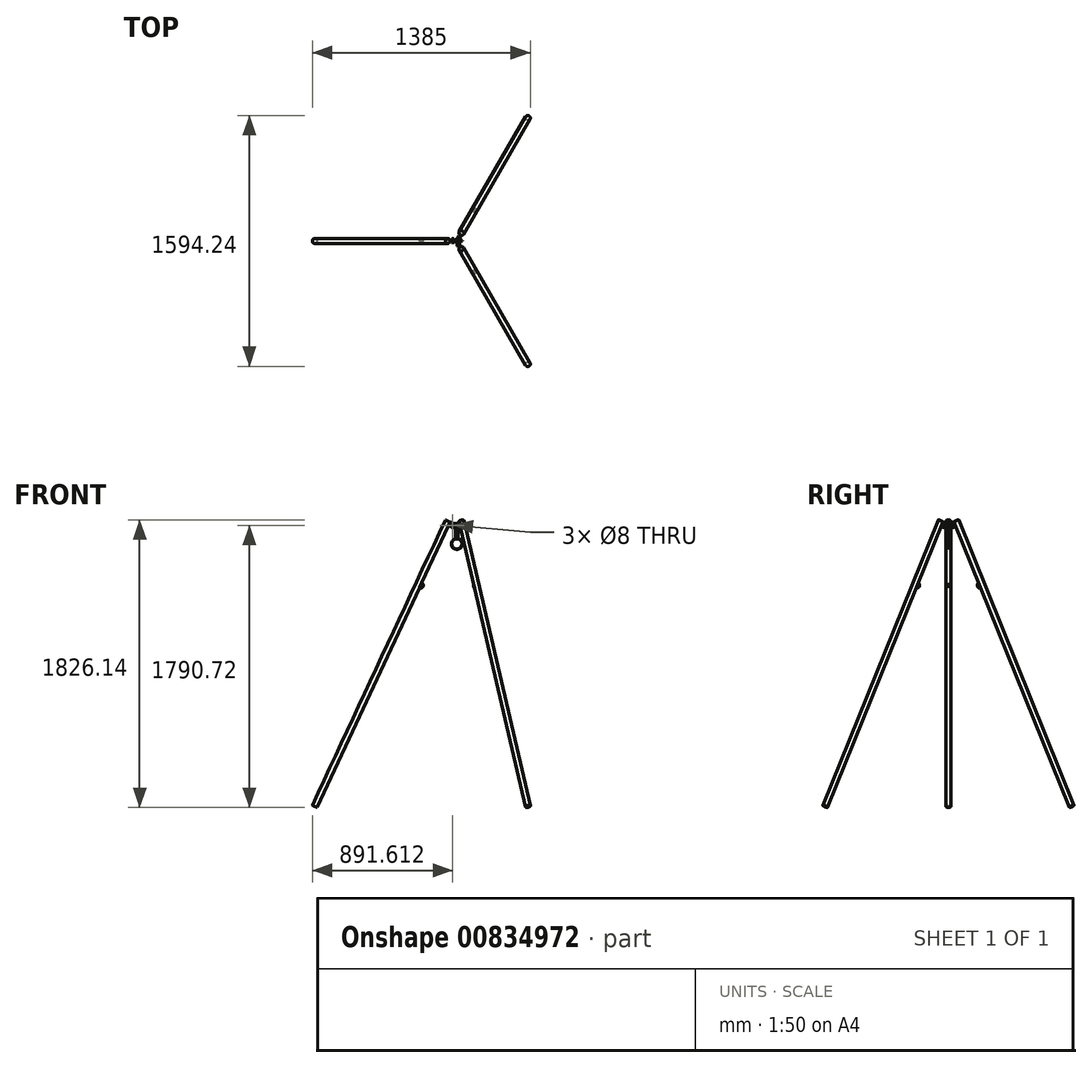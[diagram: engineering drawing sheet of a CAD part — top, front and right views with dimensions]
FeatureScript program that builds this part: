
annotation { "Feature Type Name" : "Feature", "Feature Type Description" : "" }
export const myFeature = defineFeature(function(context is Context, id is Id, definition is map)
    precondition{}
    {
        {
            assignVariable(context, id + "F0", {"variableType" : VariableType.LENGTH, "name" : "PipeLength", "lengthValue" : 2000 * mm});
        }
        {
            assignVariable(context, id + "F1", {"variableType" : VariableType.ANGLE, "name" : "LegAngle", "angleValue" : 25 * degree});
        }
        {
            var Q0;
            Q0=qCreatedBy(makeId("Right.planeOp"),FACE);
            var sketch = newSketch(context, id + "F2", { "sketchPlane" : qUnion([Q0])});
            skLineSegment(sketch, "E0", {"start": v(0, 0) * mm, "end": v(-174.54, 0) * mm, "construction": true});
            skLineSegment(sketch, "E1", {"start": v(0, 0) * mm, "end": v(0, 119.44) * mm, "construction": true});
            skSolve(sketch);
        }
        {
            var Q0;
            Q0=sQuery(id+"F2.wireOp",EDGE,"E0");
            var Q1;
            Q1=sQuery(id+"F2.wireOp",VERTEX,"E1.end");
            cPlane(context, id + "F3", {"entities" : qUnion([Q0, Q1]), "cplaneType" : CPlaneType.LINE_ANGLE, "offset" : 25 * mm, "angle" : 90 * degree - getVariable(context, 'LegAngle'), "width" : 150 * mm, "height" : 150 * mm});
        }
        {
            var Q0;
            Q0=qCreatedBy(id+"F3.planeOp",FACE);
            var sketch = newSketch(context, id + "F4", { "sketchPlane" : qUnion([Q0])});
            skCircle(sketch, "E2", {"center": v(-64, 0) * mm, "radius": 16 * mm});
            skSolve(sketch);
        }
        {
            var Q0;
            Q0=qSketchRegion(id+"F4",true);
            extrude(context, id + "F5", {"entities" : qUnion([Q0]), "depth" : getVariable(context, 'PipeLength'), "offsetDistance" : 25 * mm});
        }
        {
            var Q0;
            Q0=qCreatedBy(makeId("Front.planeOp"),FACE);
            var sketch = newSketch(context, id + "F6", { "sketchPlane" : qUnion([Q0])});
            skCircle(sketch, "E3", {"center": v(-26.13, -1.6) * mm, "radius": 4 * mm});
            skArc(sketch, "E4", {"start": v(-31.41, -12.94) * mm, "mid": v(-14.8, -6.9) * mm, "end": v(-20.85, 9.72) * mm});
            skLineSegment(sketch, "E5", {"start": v(-43.5, 20.29) * mm, "end": v(-888.74, -1792.33) * mm, "construction": true});
            skLineSegment(sketch, "E6.0", {"start": v(-43.5, 20.29) * mm, "end": v(-72.5, 33.8) * mm, "construction": true});
            skLineSegment(sketch, "E7", {"start": v(-20.85, 9.72) * mm, "end": v(-43.5, 20.29) * mm});
            skLineSegment(sketch, "E8", {"start": v(-31.41, -12.94) * mm, "end": v(-54.07, -2.37) * mm});
            skLineSegment(sketch, "E9", {"start": v(-54.07, -2.37) * mm, "end": v(-43.5, 20.29) * mm});
            skSolve(sketch);
        }
        {
            var Q0;
            Q0 = qSketchRegion(id + "F6", true);
            extrude(context, id + "F7", {"entities" : qUnion([Q0]), "operationType" : NewBodyOperationType.ADD, "endBound" : BoundingType.SYMMETRIC, "depth" : 3 * mm, "offsetDistance" : 25 * mm});
        }
        {
            var Q0;
            Q0=qCreatedBy(makeId("Front.planeOp"),FACE);
            var sketch = newSketch(context, id + "F8", { "sketchPlane" : qUnion([Q0])});
            skLineSegment(sketch, "E10", {"start": v(-43.5, 20.29) * mm, "end": v(-888.74, -1792.33) * mm, "construction": true});
            skArc(sketch, "E11", {"start": v(-224.38, -367.61) * mm, "mid": v(-217.13, -387.55) * mm, "end": v(-237.06, -394.8) * mm});
            skArc(sketch, "E12", {"start": v(-223.12, -364.9) * mm, "mid": v(-214.4, -388.82) * mm, "end": v(-238.33, -397.52) * mm});
            skLineSegment(sketch, "E13", {"start": v(-223.12, -364.9) * mm, "end": v(-224.38, -367.61) * mm});
            skLineSegment(sketch, "E14", {"start": v(-237.06, -394.8) * mm, "end": v(-238.33, -397.52) * mm});
            skSolve(sketch);
        }
        {
            var Q0;
            Q0 = qSketchRegion(id + "F8", true);
            extrude(context, id + "F9", {"entities" : qUnion([Q0]), "endBound" : BoundingType.SYMMETRIC, "depth" : 3 * mm, "offsetDistance" : 25 * mm});
        }
        {
            var Q0;
            Q0=makeQuery(id+"F5.opExtrude","SWEPT_BODY",BODY,{"disambiguationData":[OSD([sQuery(id+"F4.wireOp",EDGE,"E2")])]});
            var Q1;
            Q1=makeQuery(id+"F7.opExtrude","SWEPT_BODY",BODY,{"disambiguationData":[OSD([sQuery(id+"F6.wireOp",EDGE,"E3"),sQuery(id+"F6.wireOp",EDGE,"E4"),sQuery(id+"F6.wireOp",EDGE,"E7"),sQuery(id+"F6.wireOp",EDGE,"E8"),sQuery(id+"F6.wireOp",EDGE,"E9")])]});
            var Q2;
            Q2=makeQuery(id+"F9.opExtrude","SWEPT_BODY",BODY,{"disambiguationData":[OSD([sQuery(id+"F8.wireOp",EDGE,"E11"),sQuery(id+"F8.wireOp",EDGE,"E12"),sQuery(id+"F8.wireOp",EDGE,"E13"),sQuery(id+"F8.wireOp",EDGE,"E14")])]});
            var Q3;
            Q3=sQuery(id+"F2.wireOp",EDGE,"E1");
            circularPattern(context, id + "F10", {"entities" : qUnion([Q0, Q1, Q2]), "axis" : qUnion([Q3]), "angle" : 360 * degree, "instanceCount" : 3, "equalSpace" : true});
        }
        {
            var Q0;
            Q0=qCreatedBy(makeId("Top.planeOp"),FACE);
            var sketch = newSketch(context, id + "F11", { "sketchPlane" : qUnion([Q0])});
            skLineSegment(sketch, "E15", {"start": v(-33.63, 1.5) * mm, "end": v(-13.63, 1.5) * mm});
            skLineSegment(sketch, "E16", {"start": v(-13.63, 1.5) * mm, "end": v(5.51, 12.55) * mm});
            skLineSegment(sketch, "E17", {"start": v(5.51, 12.55) * mm, "end": v(15.51, 29.87) * mm});
            skLineSegment(sketch, "E18", {"start": v(15.51, 29.87) * mm, "end": v(12.92, 31.37) * mm});
            skLineSegment(sketch, "E19", {"start": v(12.92, 31.37) * mm, "end": v(3.32, 14.75) * mm});
            skLineSegment(sketch, "E20", {"start": v(3.32, 14.75) * mm, "end": v(-14.43, 4.5) * mm});
            skLineSegment(sketch, "E21", {"start": v(-14.43, 4.5) * mm, "end": v(-33.63, 4.5) * mm});
            skLineSegment(sketch, "E22", {"start": v(-33.63, 4.5) * mm, "end": v(-33.63, 1.5) * mm});
            skLineSegment(sketch, "E23", {"start": v(-13.63, 1.5) * mm, "end": v(-13.63, -1.5) * mm, "construction": true});
            skLineSegment(sketch, "E24", {"start": v(8.11, 11.05) * mm, "end": v(5.51, 12.55) * mm, "construction": true});
            skSolve(sketch);
        }
        {
            var Q0;
            Q0 = qSketchRegion(id + "F11", true);
            extrude(context, id + "F12", {"entities" : qUnion([Q0]), "endBound" : BoundingType.SYMMETRIC, "depth" : 25 * mm, "offsetDistance" : 25 * mm});
        }
        {
            var Q0;
            Q0=makeQuery(id+"F12.opExtrude","SWEPT_FACE",FACE,{"disambiguationData":[OSD([sQuery(id+"F11.wireOp",EDGE,"E15")])]});
            var sketch = newSketch(context, id + "F13", { "sketchPlane" : qUnion([Q0])});
            skCircle(sketch, "E25.0", {"center": v(-26.13, -1.6) * mm, "radius": 4 * mm});
            skSolve(sketch);
        }
        {
            var Q0;
            Q0 = qSketchRegion(id + "F13", true);
            extrude(context, id + "F14", {"entities" : qUnion([Q0]), "operationType" : NewBodyOperationType.REMOVE, "oppositeDirection" : true, "depth" : 25 * mm, "offsetDistance" : 25 * mm});
        }
        {
            var Q0;
            Q0=makeQuery(id+"F12.opExtrude","SWEPT_FACE",FACE,{"disambiguationData":[OSD([sQuery(id+"F11.wireOp",EDGE,"E17")])]});
            var sketch = newSketch(context, id + "F15", { "sketchPlane" : qUnion([Q0])});
            skCircle(sketch, "E26.0", {"center": v(26.13, -1.6) * mm, "radius": 4 * mm});
            skSolve(sketch);
        }
        {
            var Q0;
            Q0 = qSketchRegion(id + "F15", true);
            extrude(context, id + "F16", {"entities" : qUnion([Q0]), "operationType" : NewBodyOperationType.REMOVE, "oppositeDirection" : true, "depth" : 25 * mm, "offsetDistance" : 25 * mm});
        }
        {
            var Q0;
            Q0=makeQuery(id+"F12.opExtrude","SWEPT_BODY",BODY,{"disambiguationData":[OSD([sQuery(id+"F11.wireOp",EDGE,"E15"),sQuery(id+"F11.wireOp",EDGE,"E16"),sQuery(id+"F11.wireOp",EDGE,"E17"),sQuery(id+"F11.wireOp",EDGE,"E18"),sQuery(id+"F11.wireOp",EDGE,"E19"),sQuery(id+"F11.wireOp",EDGE,"E20"),sQuery(id+"F11.wireOp",EDGE,"E21"),sQuery(id+"F11.wireOp",EDGE,"E22")])]});
            var Q1;
            Q1=sQuery(id+"F2.wireOp",EDGE,"E1");
            circularPattern(context, id + "F17", {"entities" : qUnion([Q0]), "axis" : qUnion([Q1]), "angle" : 360 * degree, "instanceCount" : 3, "equalSpace" : true});
        }
        {
            var Q0;
            Q0=makeQuery(id+"F17.opPattern","COPY",FACE,{"derivedFrom":makeQuery(id+"F12.opExtrude","SWEPT_FACE",FACE,{"disambiguationData":[OSD([sQuery(id+"F11.wireOp",EDGE,"E19")])]}),"instanceName":"1"});
            var sketch = newSketch(context, id + "F18", { "sketchPlane" : qUnion([Q0])});
            skCircle(sketch, "E27.0", {"center": v(-26.13, -1.6) * mm, "radius": 4 * mm});
            skSolve(sketch);
        }
        {
            var Q0;
            Q0 = qSketchRegion(id + "F18", true);
            extrude(context, id + "F19", {"entities" : qUnion([Q0]), "oppositeDirection" : true, "depth" : (3 * 3 + 10) * mm, "offsetDistance" : 25 * mm});
        }
        {
            var Q0;
            Q0=makeQuery(id+"F19.opExtrude","CAP_FACE",FACE,{"disambiguationData":[OSD([sQuery(id+"F18.wireOp",EDGE,"E27.0")])],"isStart":true});
            var sketch = newSketch(context, id + "F20", { "sketchPlane" : qUnion([Q0])});
            skCircle(sketch, "E28.cCircle", {"center": v(-26.13, -1.6) * mm, "radius": 6.5 * mm, "construction": true});
            skLineSegment(sketch, "E28.0", {"start": v(-19.09, -4.2) * mm, "end": v(-24.86, -9) * mm});
            skLineSegment(sketch, "E28.1", {"start": v(-24.86, -9) * mm, "end": v(-31.9, -6.4) * mm});
            skLineSegment(sketch, "E28.2", {"start": v(-31.9, -6.4) * mm, "end": v(-33.17, 1) * mm});
            skLineSegment(sketch, "E28.3", {"start": v(-33.17, 1) * mm, "end": v(-27.4, 5.79) * mm});
            skLineSegment(sketch, "E28.4", {"start": v(-27.4, 5.79) * mm, "end": v(-20.36, 3.19) * mm});
            skLineSegment(sketch, "E28.5", {"start": v(-20.36, 3.19) * mm, "end": v(-19.09, -4.2) * mm});
            skPoint(sketch, "E28.0.midPoint", {"position": v(-21.97, -6.6) * mm});
            skSolve(sketch);
        }
        {
            var Q0;
            Q0 = qSketchRegion(id + "F20", true);
            extrude(context, id + "F21", {"entities" : qUnion([Q0]), "operationType" : NewBodyOperationType.ADD, "depth" : 6 * mm, "offsetDistance" : 25 * mm});
        }
        {
            var Q0;
            Q0=makeQuery(id+"F12.opExtrude","SWEPT_FACE",FACE,{"disambiguationData":[OSD([sQuery(id+"F11.wireOp",EDGE,"E21")])]});
            var sketch = newSketch(context, id + "F22", { "sketchPlane" : qUnion([Q0])});
            skCircle(sketch, "E29.0.0", {"center": v(26.13, -1.6) * mm, "radius": 4 * mm});
            skCircle(sketch, "E30.cCircle", {"center": v(26.13, -1.6) * mm, "radius": 6.5 * mm, "construction": true});
            skLineSegment(sketch, "E30.0", {"start": v(22.38, 4.9) * mm, "end": v(29.88, 4.9) * mm});
            skLineSegment(sketch, "E30.1", {"start": v(29.88, 4.9) * mm, "end": v(33.63, -1.6) * mm});
            skLineSegment(sketch, "E30.2", {"start": v(33.63, -1.6) * mm, "end": v(29.88, -8.1) * mm});
            skLineSegment(sketch, "E30.3", {"start": v(29.88, -8.1) * mm, "end": v(22.38, -8.1) * mm});
            skLineSegment(sketch, "E30.4", {"start": v(22.38, -8.1) * mm, "end": v(18.62, -1.6) * mm});
            skLineSegment(sketch, "E30.5", {"start": v(18.62, -1.6) * mm, "end": v(22.38, 4.9) * mm});
            skPoint(sketch, "E30.0.midPoint", {"position": v(26.13, 4.9) * mm});
            skSolve(sketch);
        }
        {
            var Q0;
            Q0 = qSketchRegion(id + "F22", true);
            extrude(context, id + "F23", {"entities" : qUnion([Q0]), "depth" : 6 * mm, "offsetDistance" : 25 * mm});
        }
        {
            var Q0;
            Q0=makeQuery(id+"F19.opExtrude","SWEPT_BODY",BODY,{"disambiguationData":[OSD([sQuery(id+"F18.wireOp",EDGE,"E27.0")])]});
            var Q1;
            Q1=makeQuery(id+"F23.opExtrude","SWEPT_BODY",BODY,{"disambiguationData":[OSD([sQuery(id+"F22.wireOp",EDGE,"E29.0.0"),sQuery(id+"F22.wireOp",EDGE,"E30.0"),sQuery(id+"F22.wireOp",EDGE,"E30.1"),sQuery(id+"F22.wireOp",EDGE,"E30.2"),sQuery(id+"F22.wireOp",EDGE,"E30.3"),sQuery(id+"F22.wireOp",EDGE,"E30.4"),sQuery(id+"F22.wireOp",EDGE,"E30.5")])]});
            var Q2;
            Q2=sQuery(id+"F2.wireOp",EDGE,"E1");
            circularPattern(context, id + "F24", {"entities" : qUnion([Q0, Q1]), "axis" : qUnion([Q2]), "angle" : 360 * degree, "instanceCount" : 3, "equalSpace" : true});
        }
        {
            var Q0;
            Q0=makeQuery(id+"F17.opPattern","COPY",FACE,{"derivedFrom":makeQuery(id+"F12.opExtrude","CAP_FACE",FACE,{"disambiguationData":[OSD([sQuery(id+"F11.wireOp",EDGE,"E15"),sQuery(id+"F11.wireOp",EDGE,"E16"),sQuery(id+"F11.wireOp",EDGE,"E17"),sQuery(id+"F11.wireOp",EDGE,"E18"),sQuery(id+"F11.wireOp",EDGE,"E19"),sQuery(id+"F11.wireOp",EDGE,"E20"),sQuery(id+"F11.wireOp",EDGE,"E21"),sQuery(id+"F11.wireOp",EDGE,"E22")])],"isStart":false}),"instanceName":"1"});
            var sketch = newSketch(context, id + "F25", { "sketchPlane" : qUnion([Q0])});
            skCircle(sketch, "E31", {"center": v(0, 0) * mm, "radius": 8 * mm});
            skSolve(sketch);
        }
        {
            var Q0;
            Q0 = qSketchRegion(id + "F25", true);
            extrude(context, id + "F26", {"entities" : qUnion([Q0]), "oppositeDirection" : true, "depth" : 100 * mm, "offsetDistance" : 25 * mm});
        }
        {
            var Q0;
            Q0=qCreatedBy(makeId("Front.planeOp"),FACE);
            var sketch = newSketch(context, id + "F27", { "sketchPlane" : qUnion([Q0])});
            skArc(sketch, "E32", {"start": v(-8, -87.5) * mm, "mid": v(0, -150.48) * mm, "end": v(8, -87.5) * mm});
            skArc(sketch, "E33", {"start": v(-8, -84.41) * mm, "mid": v(0, -153.48) * mm, "end": v(8, -84.41) * mm});
            skLineSegment(sketch, "E34.0", {"start": v(-8, -87.5) * mm, "end": v(8, -87.5) * mm, "construction": true});
            skLineSegment(sketch, "E35", {"start": v(-8, -87.5) * mm, "end": v(-8, 12.5) * mm, "construction": true});
            skLineSegment(sketch, "E36", {"start": v(8, 12.5) * mm, "end": v(8, -87.5) * mm, "construction": true});
            skLineSegment(sketch, "E37", {"start": v(-8, -87.5) * mm, "end": v(-8, -84.41) * mm});
            skLineSegment(sketch, "E38", {"start": v(8, -84.41) * mm, "end": v(8, -87.5) * mm});
            skSolve(sketch);
        }
        {
            var Q0;
            Q0 = qSketchRegion(id + "F27", true);
            extrude(context, id + "F28", {"entities" : qUnion([Q0]), "endBound" : BoundingType.SYMMETRIC, "depth" : 3 * mm, "offsetDistance" : 25 * mm});
        }
    });
